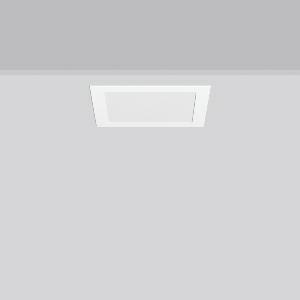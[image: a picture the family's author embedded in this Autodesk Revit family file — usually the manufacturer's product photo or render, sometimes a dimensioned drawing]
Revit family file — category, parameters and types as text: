
# Revit family: toledo_flat_square_e_672243_002_3d22
name_source: partatom
category: Lighting Fixtures
units: mm (PartAtom-declared; Revit-internal decimal feet)

## family parameters
Cut with Voids When Loaded = No
Host = Face
Light Source = No
Part Type = Normal
Room Calculation Point = No
Round Connector Dimension = Use Diameter
Shared = No

## types (1)
- TOLEDO FLAT square E (1 x LED Modul 830, 1600 lm, 3000)
    Apparent Load = 18 VA
    CIE Flux Codes = 48 80 96 100 100
    Color Rendering = 80
    Color Temperature = 3000
    Default Elevation = 1800 mm
    Description = Series: TOLEDO FLAT square
Square recessed downlight. For escape route illumination. Housing: die-cast aluminium, powder-coated. Lightguide and diffuser made of non-yellowing plastic (PMMA). Diffuser opal matt plastic. Ceiling installation with spring system. Including separate LED converter with connecting cable 250 mm. Suitable for connection to central battery systems. External driver with simple plug-in locking system. 
Colour: white
Length: 225 mm
Width: 225 mm
Height: 3 mm
Cut-out length: 208 mm
Cut-out width: 208 mm
Recess height: 35 mm
Luminaire: recess height: 31-51 mm
Weight: 0.653 kg
Operating mode: maintained power mode
Lamp: LED
Socket: without socket
Colour temperature: 3000K
Colour rendering index (CRI): 80
System power: 18 W
Rated luminous flux: 1600 lm
Luminous flux, emergency: 1600 lm
System power, emergency: 18 W
Control gear: Regulated power supply
Protection class: II
Type of protection: IP 54
    Height = 0 mm  [stored 0 ft]
    Lamp = 1 x LED Modul 830
    Lamp Light Flux = 1600 lm
    Lamp count = 1
    Length = 225 mm
    Lifetime = 50000 h
    Luminous efficacy = 89 lm/W
    Manufacturer = RZB
    ModVariant = No
    Model = 672243.002
    Mounting Place = Ceiling
    Mounting Type = Recessed
    Number of Poles = 1
    OnlyDefault = Yes
    Power Factor = 1
    Product Name = TOLEDO FLAT square E
    Product group = Recessed downlights
    ProductGroupID = 402
    Protection Class = Protection class II
    Protection Degree = IP 40
    RLX_Detail_Level = 1
    RLX_Emergency_Light_Flux = 1600 lm
    RLX_Emergency_Type = 3
    RLX_Emergency_Type_DB = Yes
    RlxData = <blob elided: 10941 chars, md5=bc671aa3>
    Socket = socket
    Standby Power = 0 W
    System Light Flux = 1600 lm
    System Power = 18 W
    Type Comments = Product without accessories
    Type Image = 901487.002.jpg
    URL = http://relux.com
    VarID = ---
    Voltage = 230 V
    Voltage Range = 220-240 V
    Weight = 0.00 kg
    Width = 225 mm

note: [stored X ft] marks values corroborated as IEEE doubles in the binary element streams (Revit-internal decimal feet)

## geometry (parser evidence)
native form markers: Sweep x10
no freeform markers — native parametric forms only
